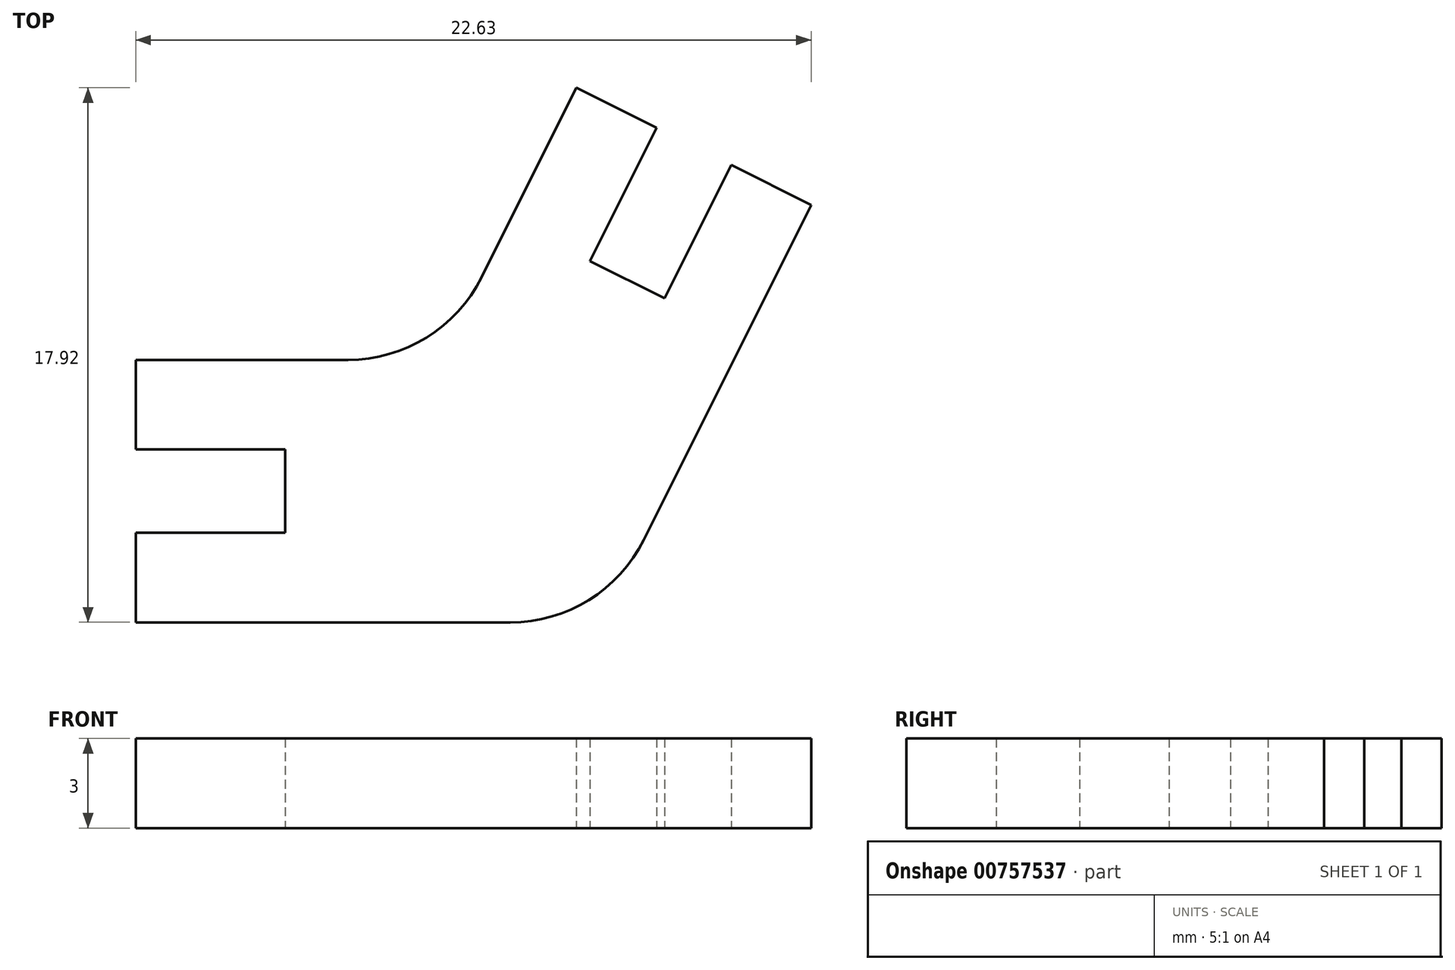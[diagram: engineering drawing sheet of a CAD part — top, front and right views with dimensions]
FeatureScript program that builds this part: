
annotation { "Feature Type Name" : "Feature", "Feature Type Description" : "" }
export const myFeature = defineFeature(function(context is Context, id is Id, definition is map)
    precondition{}
    {
        {
            var Q0;
            Q0=qCreatedBy(makeId("Top.planeOp"),FACE);
            var sketch = newSketch(context, id + "F0", { "sketchPlane" : qUnion([Q0])});
            skLineSegment(sketch, "E0.0.3", {"start": v(-2.5, -1.25) * mm, "end": v(-2.5, -4.05) * mm});
            skLineSegment(sketch, "E1.MirrorCS", {"start": v(-2.5, -4.05) * mm, "end": v(-7.5, -4.05) * mm});
            skLineSegment(sketch, "E2", {"start": v(-7.5, -1.25) * mm, "end": v(-7.5, 1.75) * mm});
            skLineSegment(sketch, "E3", {"start": v(-7.5, 1.75) * mm, "end": v(-0.39, 1.75) * mm});
            skLineSegment(sketch, "E4", {"start": v(-7.5, -1.25) * mm, "end": v(-2.5, -1.25) * mm});
            skLineSegment(sketch, "E5", {"start": v(-7.5, -4.05) * mm, "end": v(-7.5, -7.05) * mm});
            skLineSegment(sketch, "E6", {"start": v(-7.5, -7.05) * mm, "end": v(5.05, -7.05) * mm});
            skLineSegment(sketch, "E7.MirrorCS", {"start": v(7.71, 5.06) * mm, "end": v(9.95, 9.53) * mm});
            skLineSegment(sketch, "E8", {"start": v(12.45, 8.28) * mm, "end": v(15.13, 6.94) * mm});
            skLineSegment(sketch, "E9", {"start": v(15.13, 6.94) * mm, "end": v(9.53, -4.29) * mm});
            skLineSegment(sketch, "E10", {"start": v(12.45, 8.28) * mm, "end": v(10.22, 3.8) * mm});
            skLineSegment(sketch, "E11", {"start": v(9.95, 9.53) * mm, "end": v(7.26, 10.87) * mm});
            skLineSegment(sketch, "E12", {"start": v(7.26, 10.87) * mm, "end": v(4.09, 4.51) * mm});
            skLineSegment(sketch, "E13", {"start": v(7.71, 5.06) * mm, "end": v(10.22, 3.8) * mm});
            skPoint(sketch, "E14.visualSharp", {"position": v(2.7, 1.75) * mm});
            skArc(sketch, "E14.filletArc", {"start": v(-0.39, 1.75) * mm, "mid": v(2.24, 2.5) * mm, "end": v(4.09, 4.51) * mm});
            skLineSegment(sketch, "E15", {"start": v(-2.5, -1.25) * mm, "end": v(7.71, 5.06) * mm, "construction": true});
            skPoint(sketch, "E16.visualSharp", {"position": v(8.14, -7.05) * mm});
            skArc(sketch, "E16.filletArc", {"start": v(5.05, -7.05) * mm, "mid": v(7.68, -6.3) * mm, "end": v(9.53, -4.29) * mm});
            skSolve(sketch);
        }
        {
            var Q0;
            Q0=qSketchRegion(id+"F0",true);
            extrude(context, id + "F1", {"entities" : qUnion([Q0]), "depth" : 3 * mm, "offsetDistance" : 25 * mm});
        }
    });
